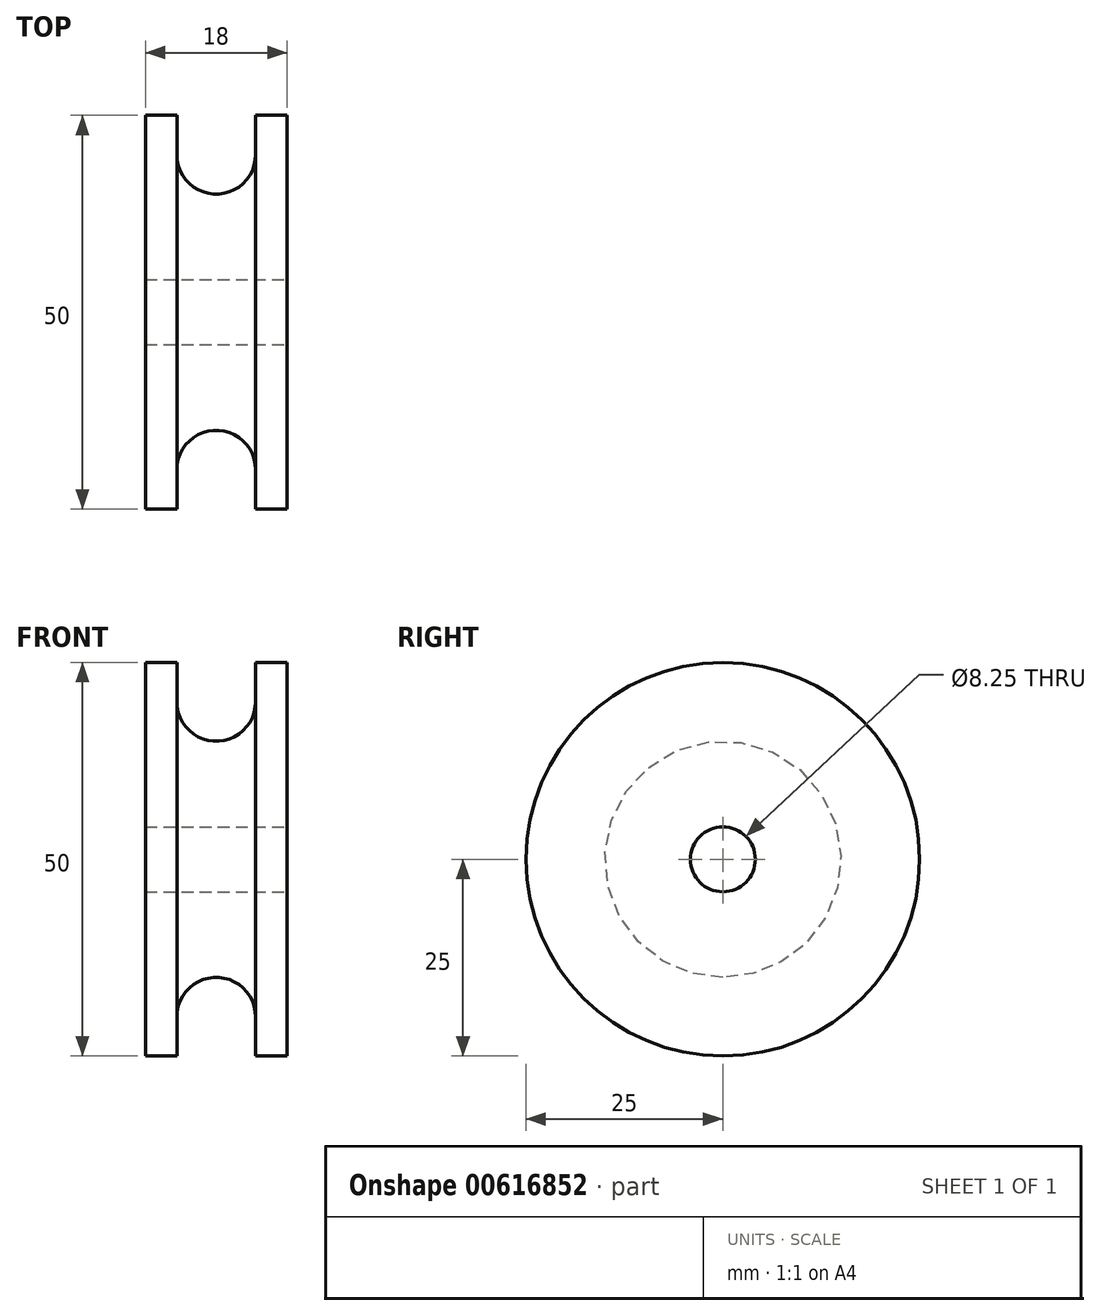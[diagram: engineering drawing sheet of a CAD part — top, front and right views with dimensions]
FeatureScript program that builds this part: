
annotation { "Feature Type Name" : "Feature", "Feature Type Description" : "" }
export const myFeature = defineFeature(function(context is Context, id is Id, definition is map)
    precondition{}
    {
        {
            var Q0;
            Q0=qCreatedBy(makeId("Front.planeOp"),FACE);
            var sketch = newSketch(context, id + "F0", { "sketchPlane" : qUnion([Q0])});
            skLineSegment(sketch, "E0", {"start": v(0, 4.12) * mm, "end": v(-18, 4.12) * mm});
            skLineSegment(sketch, "E1", {"start": v(-18, 4.12) * mm, "end": v(-18, 25) * mm});
            skLineSegment(sketch, "E2", {"start": v(-18, 25) * mm, "end": v(-14, 25) * mm});
            skLineSegment(sketch, "E3", {"start": v(-14, 25) * mm, "end": v(-14, 20) * mm});
            skLineSegment(sketch, "E4", {"start": v(0, 4.13) * mm, "end": v(0, 25) * mm});
            skLineSegment(sketch, "E5", {"start": v(0, 25) * mm, "end": v(-4, 25) * mm});
            skLineSegment(sketch, "E6", {"start": v(-4, 25) * mm, "end": v(-4, 20) * mm});
            skArc(sketch, "E7", {"start": v(-14, 20) * mm, "mid": v(-9, 15) * mm, "end": v(-4, 20) * mm});
            skLineSegment(sketch, "E8", {"start": v(0, 0) * mm, "end": v(-18.06, 0) * mm, "construction": true});
            skSolve(sketch);
        }
        {
            var Q0;
            Q0 = qSketchRegion(id + "F0", true);
            var Q1;
            Q1=sQuery(id+"F0.wireOp",EDGE,"E8");
            revolve(context, id + "F1", {"surfaceOperationType" : NewSurfaceOperationType.NEW, "entities" : qUnion([Q0]), "axis" : qUnion([Q1]), "revolveType" : RevolveType.FULL});
        }
    });
